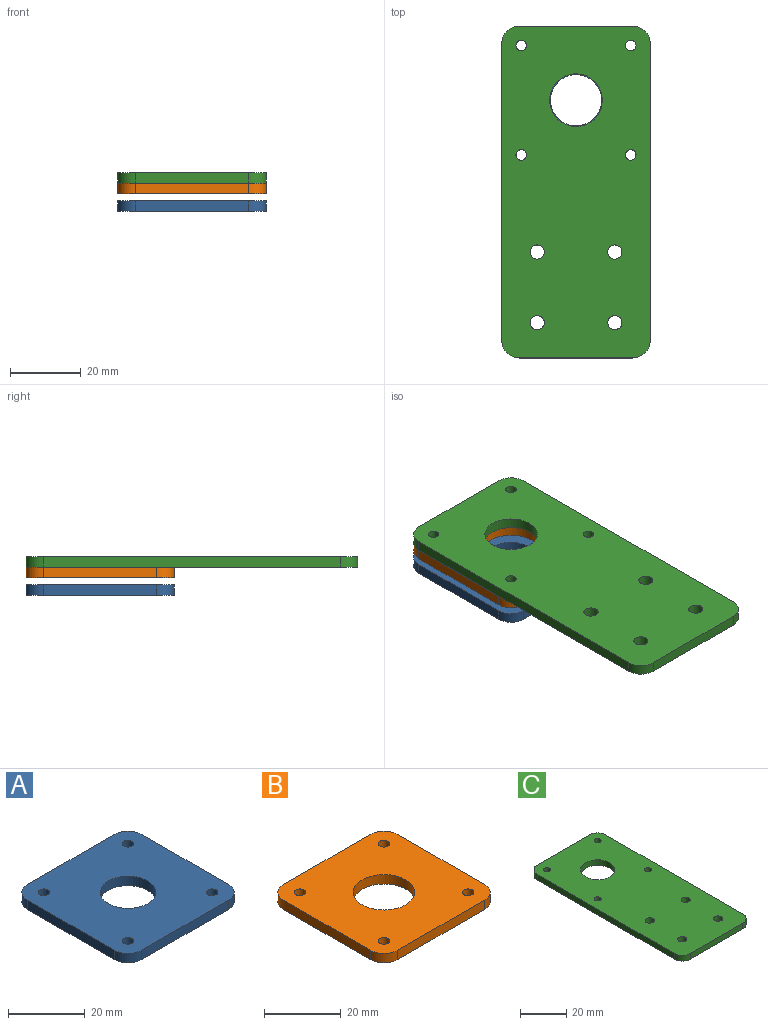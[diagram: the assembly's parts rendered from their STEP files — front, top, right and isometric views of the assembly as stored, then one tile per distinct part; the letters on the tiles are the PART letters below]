
ASSEMBLY  parts=3 mates=2
PART A: 15 faces, bbox 42x42x3 mm
  f0: plane 32x3mm, normal (0,-1,0), area 96mm2, adj f4,f5,f11,f14
  f1: plane 32x3mm, normal (1,0,0), area 96mm2, adj f4,f5,f11,f12
  f2: plane 32x3mm, normal (0,1,0), area 96mm2, adj f4,f5,f12,f13
  f3: plane 32x3mm, normal (-1,0,0), area 96mm2, adj f4,f5,f13,f14
  f4: plane 42x42mm, normal (0,0,1), area 1549.1mm2, adj f0,f1,f2,f3,f6,f7,f8,f9
  f5: plane 42x42mm, normal (0,0,-1), area 1549.1mm2, adj f0,f1,f2,f3,f6,f7,f8,f9
  f6: cylinder r=7.25mm len=14.5mm, axis (0,0,1), area 136.7mm2, adj f4,f5
  f7: cylinder r=1.5mm len=3mm, axis (0,0,-1), area 28.3mm2, adj f4,f5
  f8: cylinder r=1.5mm len=3mm, axis (0,0,-1), area 28.3mm2, adj f4,f5
  f9: cylinder r=1.5mm len=3mm, axis (0,0,-1), area 28.3mm2, adj f4,f5
  f10: cylinder r=1.5mm len=3mm, axis (0,0,-1), area 28.3mm2, adj f4,f5
  f11: cylinder r=5mm len=5mm, axis (0,0,-1), area 23.6mm2, adj f0,f1,f4,f5
  f12: cylinder r=5mm len=5mm, axis (0,0,1), area 23.6mm2, adj f1,f2,f4,f5
  f13: cylinder r=5mm len=5mm, axis (0,0,-1), area 23.6mm2, adj f2,f3,f4,f5
  f14: cylinder r=5mm len=5mm, axis (0,0,1), area 23.6mm2, adj f0,f3,f4,f5
PART B: 15 faces, bbox 42x42x3 mm
  f0: plane 32x3mm, normal (0,-1,0), area 96mm2, adj f4,f5,f12,f14
  f1: plane 32x3mm, normal (1,0,0), area 96mm2, adj f4,f5,f13,f14
  f2: plane 32x3mm, normal (0,1,0), area 96mm2, adj f4,f5,f11,f13
  f3: plane 32x3mm, normal (-1,0,0), area 96mm2, adj f4,f5,f11,f12
  f4: plane 42x42mm, normal (0,0,1), area 1513.2mm2, adj f0,f1,f2,f3,f6,f7,f8,f9
  f5: plane 42x42mm, normal (0,0,-1), area 1513.2mm2, adj f0,f1,f2,f3,f6,f7,f8,f9
  f6: cylinder r=8mm len=16mm, axis (0,0,1), area 150.8mm2, adj f4,f5
  f7: cylinder r=1.5mm len=3mm, axis (0,0,-1), area 28.3mm2, adj f4,f5
  f8: cylinder r=1.5mm len=3mm, axis (0,0,-1), area 28.3mm2, adj f4,f5
  f9: cylinder r=1.5mm len=3mm, axis (0,0,-1), area 28.3mm2, adj f4,f5
  f10: cylinder r=1.5mm len=3mm, axis (0,0,-1), area 28.3mm2, adj f4,f5
  f11: cylinder r=5mm len=5mm, axis (0,0,-1), area 23.6mm2, adj f2,f3,f4,f5
  f12: cylinder r=5mm len=5mm, axis (0,0,1), area 23.6mm2, adj f0,f3,f4,f5
  f13: cylinder r=5mm len=5mm, axis (0,0,1), area 23.6mm2, adj f1,f2,f4,f5
  f14: cylinder r=5mm len=5mm, axis (0,0,-1), area 23.6mm2, adj f0,f1,f4,f5
PART C: 19 faces, bbox 42x94x3 mm
  f0: plane 84x3mm, normal (-1,0,0), area 252mm2, adj f4,f5,f11,f12
  f1: plane 32x3mm, normal (0,-1,0), area 96mm2, adj f4,f5,f12,f13
  f2: plane 84x3mm, normal (1,0,0), area 252mm2, adj f4,f5,f10,f13
  f3: plane 32x3mm, normal (0,1,0), area 96mm2, adj f4,f5,f10,f11
  f4: plane 94x42mm, normal (0,0,1), area 3673.6mm2, adj f0,f1,f2,f3,f6,f7,f8,f9
  f5: plane 94x42mm, normal (0,0,-1), area 3673.6mm2, adj f0,f1,f2,f3,f6,f7,f8,f9
  f6: cylinder r=1.5mm len=3mm, axis (0,0,-1), area 28.3mm2, adj f4,f5
  f7: cylinder r=1.5mm len=3mm, axis (0,0,-1), area 28.3mm2, adj f4,f5
  f8: cylinder r=1.5mm len=3mm, axis (0,0,-1), area 28.3mm2, adj f4,f5
  f9: cylinder r=1.5mm len=3mm, axis (0,0,-1), area 28.3mm2, adj f4,f5
  f10: cylinder r=5mm len=5mm, axis (0,0,1), area 23.6mm2, adj f2,f3,f4,f5
  f11: cylinder r=5mm len=5mm, axis (0,0,-1), area 23.6mm2, adj f0,f3,f4,f5
  f12: cylinder r=5mm len=5mm, axis (0,0,-1), area 23.6mm2, adj f0,f1,f4,f5
  f13: cylinder r=5mm len=5mm, axis (0,0,1), area 23.6mm2, adj f1,f2,f4,f5
  f14: cylinder r=7.45mm len=14.9mm, axis (0,0,-1), area 140.4mm2, adj f4,f5
  f15: cylinder r=2mm len=4mm, axis (0,0,-1), area 37.7mm2, adj f4,f5
  f16: cylinder r=2mm len=4mm, axis (0,0,-1), area 37.7mm2, adj f4,f5
  f17: cylinder r=2mm len=4mm, axis (0,0,-1), area 37.7mm2, adj f4,f5
  f18: cylinder r=2mm len=4mm, axis (0,0,-1), area 37.7mm2, adj f4,f5
PLACE A t=(-14.06,-11.93,-63.08)mm
PLACE B t=(-14.06,-11.93,-53.88)mm
PLACE C t=(-14.06,-11.93,-44.58)mm
MATE fastened B.f6 <-> C.f14  axis (0,0,1) through (-14.06,-11.93,-35.88)mm
MATE fastened C.f14 <-> A.f6  axis (0,0,-1) through (-14.06,-11.93,-35.88)mm
